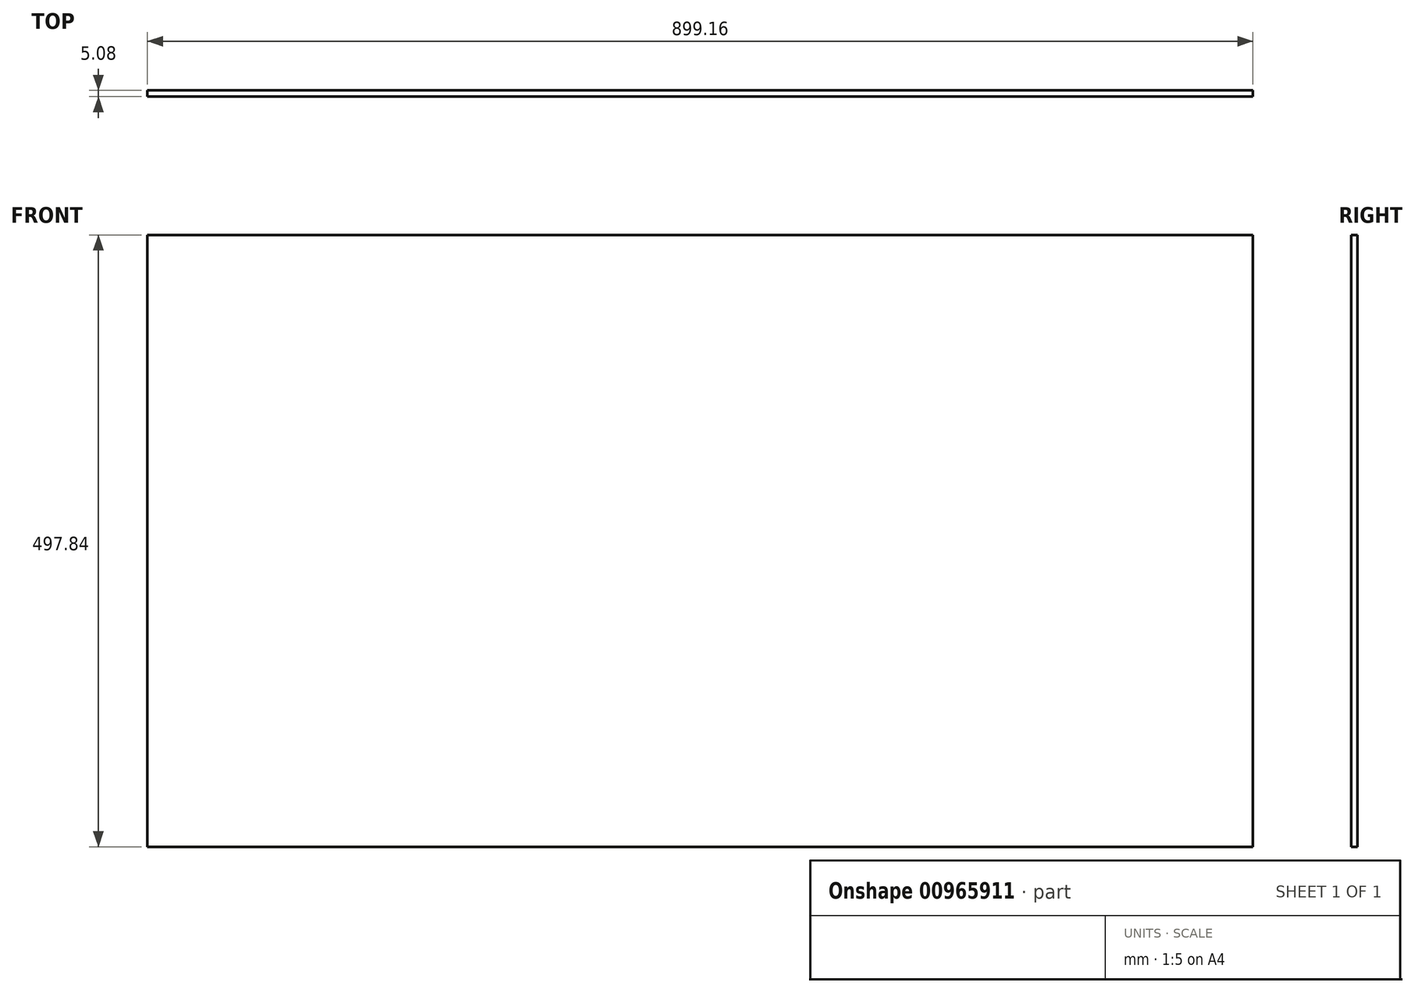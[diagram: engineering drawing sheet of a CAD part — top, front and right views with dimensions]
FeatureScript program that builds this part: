
annotation { "Feature Type Name" : "Feature", "Feature Type Description" : "" }
export const myFeature = defineFeature(function(context is Context, id is Id, definition is map)
    precondition{}
    {
        {
            var Q0;
            Q0=qCreatedBy(makeId("Front.planeOp"),FACE);
            var sketch = newSketch(context, id + "F0", { "sketchPlane" : qUnion([Q0])});
            skLineSegment(sketch, "E0.bottom", {"start": v(0, 0) * mm, "end": v(899.16, 0) * mm});
            skLineSegment(sketch, "E0.top", {"start": v(0, -497.84) * mm, "end": v(899.16, -497.84) * mm});
            skLineSegment(sketch, "E0.left", {"start": v(0, 0) * mm, "end": v(0, -497.84) * mm});
            skLineSegment(sketch, "E0.right", {"start": v(899.16, 0) * mm, "end": v(899.16, -497.84) * mm});
            skSolve(sketch);
        }
        {
            var Q0;
            Q0=makeQuery(id+"F0.imprint","IMPRINT",FACE,{"disambiguationData":[TD([[makeQuery(id+"F0.imprint","IMPRINT",EDGE,{"derivedFrom":sQuery(id+"F0.wireOp",EDGE,"E0.bottom")}),-1.0]])]});
            extrude(context, id + "F1", {"entities" : qUnion([Q0]), "depth" : 5.08 * mm, "offsetDistance" : 25.4 * mm});
        }
    });
